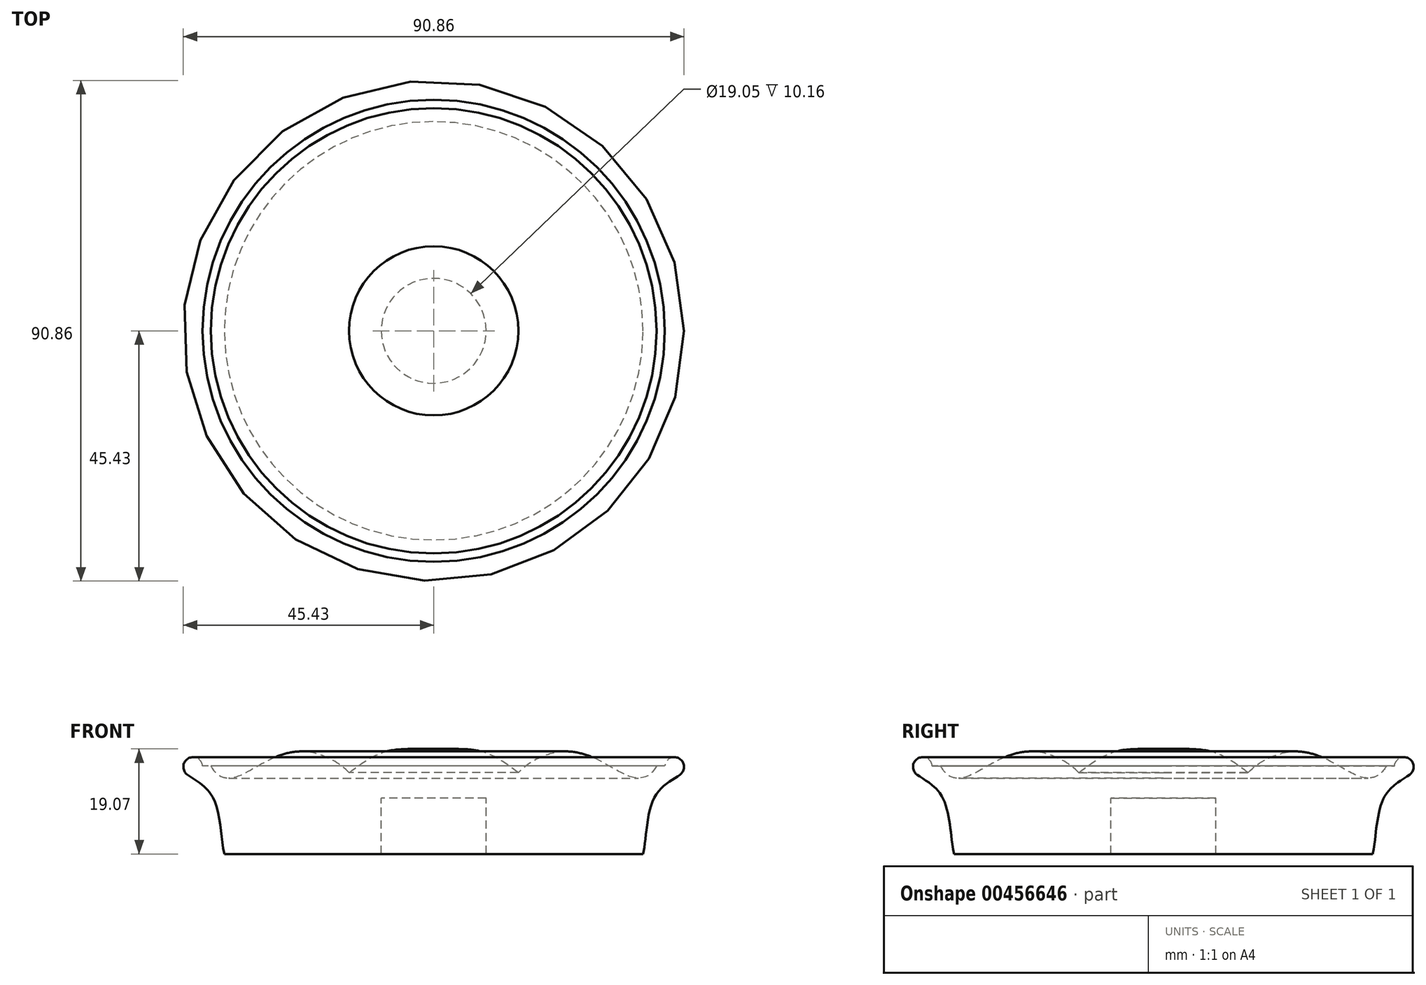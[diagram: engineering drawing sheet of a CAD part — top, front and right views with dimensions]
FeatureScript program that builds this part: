
annotation { "Feature Type Name" : "Feature", "Feature Type Description" : "" }
export const myFeature = defineFeature(function(context is Context, id is Id, definition is map)
    precondition{}
    {
        {
            var Q0;
            Q0=qCreatedBy(makeId("Front.planeOp"),FACE);
            var sketch = newSketch(context, id + "F0", { "sketchPlane" : qUnion([Q0])});
            skLineSegment(sketch, "E0", {"start": v(0, 0) * mm, "end": v(9.52, 0) * mm});
            skLineSegment(sketch, "E1", {"start": v(9.52, 0) * mm, "end": v(9.52, -10.16) * mm});
            skLineSegment(sketch, "E2", {"start": v(9.53, -10.16) * mm, "end": v(37.99, -10.16) * mm});
            skFitSpline(sketch, "E3", {"points": [v(37.99, -10.16) * mm, v(40, 0) * mm, v(44.71, 4.26) * mm], "startDerivative": vector(2.99, 11.26) * mm, "endDerivative": vector(10.38, 7.6) * mm});
            skArc(sketch, "E4", {"start": v(44.71, 4.26) * mm, "mid": v(44.54, 7.18) * mm, "end": v(41.94, 5.82) * mm});
            skLineSegment(sketch, "E5", {"start": v(41.94, 5.82) * mm, "end": v(40.44, 5.82) * mm});
            skFitSpline(sketch, "E6", {"points": [v(40.44, 5.82) * mm, v(36.75, 3.65) * mm, v(31.85, 5.82) * mm, v(23.84, 8.45) * mm, v(15.36, 4.59) * mm], "startDerivative": vector(-14.27, -27) * mm, "endDerivative": vector(-18.73, -20.79) * mm});
            skFitSpline(sketch, "E7", {"points": [v(15.36, 4.59) * mm, v(9.24, 8.26) * mm, v(0, 8.9) * mm], "startDerivative": vector(-12.6, 9.7) * mm, "endDerivative": vector(-23.65, -0.01) * mm});
            skLineSegment(sketch, "E8", {"start": v(0, 8.9) * mm, "end": v(0, 0) * mm});
            skSolve(sketch);
        }
        {
            var Q0;
            Q0=makeQuery(id+"F0.imprint","IMPRINT",FACE,{"disambiguationData":[TD([[makeQuery(id+"F0.imprint","IMPRINT",EDGE,{"derivedFrom":sQuery(id+"F0.wireOp",EDGE,"E0")}),1.0]])]});
            var Q1;
            Q1=sQuery(id+"F0.wireOp",EDGE,"E8");
            revolve(context, id + "F1", {"entities" : qUnion([Q0]), "axis" : qUnion([Q1]), "revolveType" : RevolveType.FULL});
        }
    });
